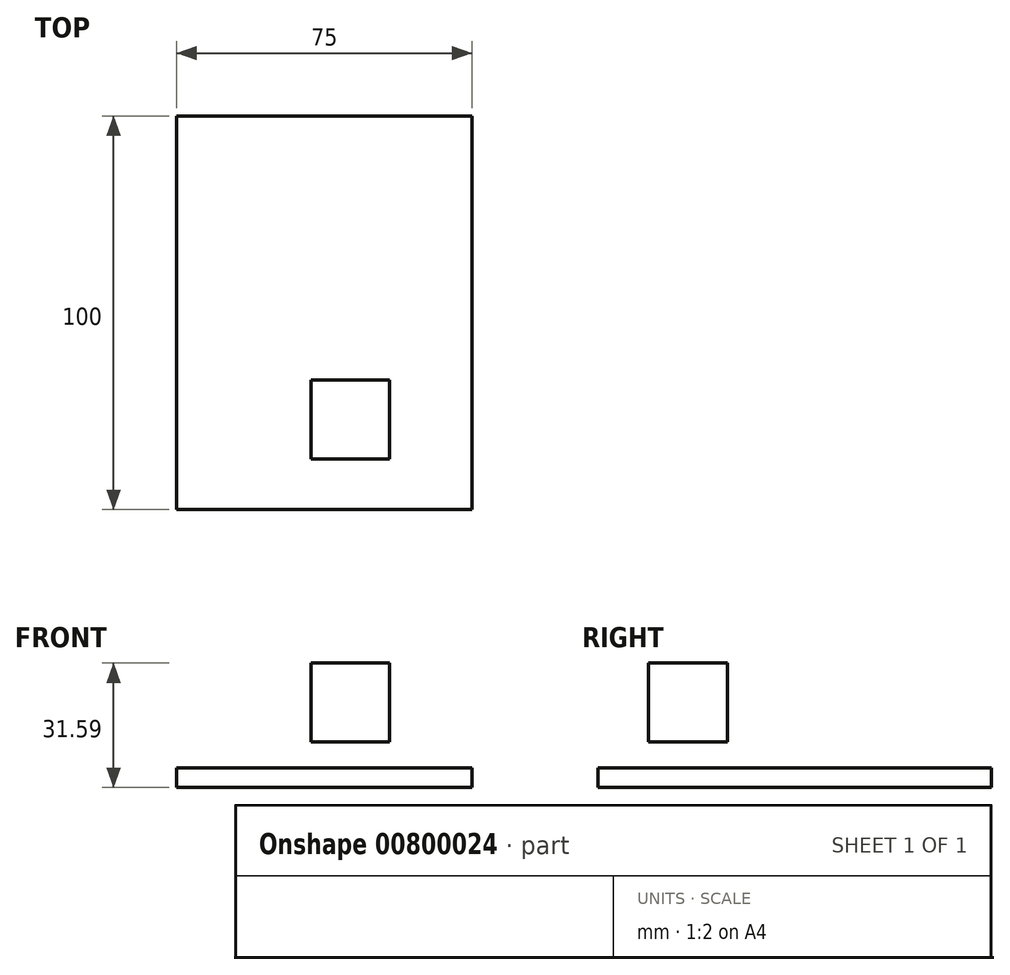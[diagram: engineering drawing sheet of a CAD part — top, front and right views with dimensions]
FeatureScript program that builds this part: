
annotation { "Feature Type Name" : "Feature", "Feature Type Description" : "" }
export const myFeature = defineFeature(function(context is Context, id is Id, definition is map)
    precondition{}
    {
        {
            var Q0;
            Q0=qCreatedBy(makeId("Front.planeOp"),FACE);
            var sketch = newSketch(context, id + "F0", { "sketchPlane" : qUnion([Q0])});
            skLineSegment(sketch, "E0.bottom", {"start": v(-18.33, 26.6) * mm, "end": v(1.67, 26.6) * mm});
            skLineSegment(sketch, "E0.top", {"start": v(-18.33, 6.6) * mm, "end": v(1.67, 6.6) * mm});
            skLineSegment(sketch, "E0.left", {"start": v(-18.33, 26.6) * mm, "end": v(-18.33, 6.6) * mm});
            skLineSegment(sketch, "E0.right", {"start": v(1.67, 26.6) * mm, "end": v(1.67, 6.6) * mm});
            skSolve(sketch);
        }
        {
            var Q0;
            Q0=makeQuery(id+"F0.imprint","IMPRINT",FACE,{"disambiguationData":[TD([[makeQuery(id+"F0.imprint","IMPRINT",EDGE,{"derivedFrom":sQuery(id+"F0.wireOp",EDGE,"E0.bottom")}),-1.0]])]});
            extrude(context, id + "F1", {"entities" : qUnion([Q0]), "depth" : 20 * mm, "offsetDistance" : 25.4 * mm});
        }
        {
            var Q0;
            Q0=qCreatedBy(makeId("Top.planeOp"),FACE);
            var sketch = newSketch(context, id + "F2", { "sketchPlane" : qUnion([Q0])});
            skLineSegment(sketch, "E1.bottom", {"start": v(-52.46, -32.91) * mm, "end": v(22.54, -32.91) * mm});
            skLineSegment(sketch, "E1.top", {"start": v(-52.46, 67.09) * mm, "end": v(22.54, 67.09) * mm});
            skLineSegment(sketch, "E1.left", {"start": v(-52.46, -32.91) * mm, "end": v(-52.46, 67.09) * mm});
            skLineSegment(sketch, "E1.right", {"start": v(22.54, -32.91) * mm, "end": v(22.54, 67.09) * mm});
            skSolve(sketch);
        }
        {
            var Q0;
            Q0=makeQuery(id+"F2.imprint","IMPRINT",FACE,{"disambiguationData":[TD([[makeQuery(id+"F2.imprint","IMPRINT",EDGE,{"derivedFrom":sQuery(id+"F2.wireOp",EDGE,"E1.bottom")}),1.0]])]});
            extrude(context, id + "F3", {"entities" : qUnion([Q0]), "oppositeDirection" : true, "depth" : 5 * mm, "offsetDistance" : 25.4 * mm});
        }
    });
